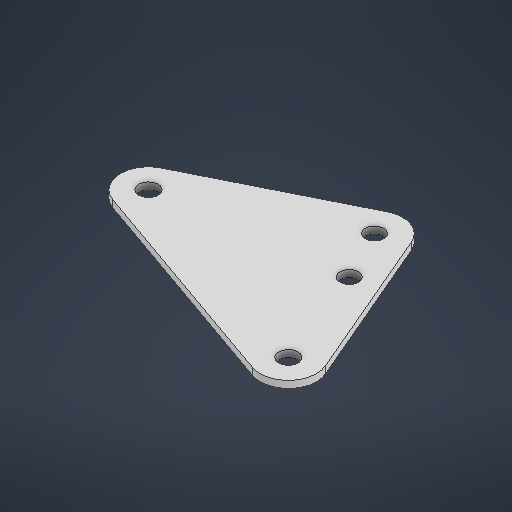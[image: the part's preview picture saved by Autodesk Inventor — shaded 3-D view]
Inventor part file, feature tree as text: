
AUTODESK INVENTOR PART (.ipt)
format: ipt  version: 2025.2 (Build 292293000, 293)  size: 193,536 bytes
history: native  units: in
note: dims shown in document units (in); Inventor stores cm internally (conversion verified against a paired STEP export)
features: extrude x1, sketch x1
ambient origin geometry x8: Origin, YZ Plane, XZ Plane, XY Plane, X Axis, Y Axis, Z Axis, Center Point
bodies: Solid1 (feature_tree)
feature tree (2):
  extrude  "Extrusion1"  [1 undecoded]
  sketch  "Sketch1"  dims[d4=0.0625in d5=0.0in]
note: 1 required parameter value undecoded (feature->parameter linkage not recoverable at this tier; creation-order binding heuristic only, values carry confidence <= 0.55)
